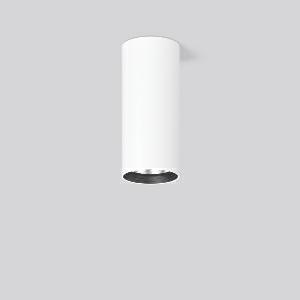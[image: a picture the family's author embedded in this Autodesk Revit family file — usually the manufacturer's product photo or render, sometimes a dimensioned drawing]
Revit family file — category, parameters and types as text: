
# Revit family: heledon_mini_a_931209_002_2_76_af3e
name_source: partatom
category: Lighting Fixtures
units: mm (PartAtom-declared; Revit-internal decimal feet)

## family parameters
Cut with Voids When Loaded = No
Host = Face
Light Source = No
Part Type = Normal
Room Calculation Point = No
Round Connector Dimension = Use Diameter
Shared = No

## types (1)
- HELEDON mini A (1 x LED Modul 927, 3300 lm, 2700)
    Apparent Load = 29 VA
    Approval mark = CE
    CIE Flux Codes = 99 100 100 100 100
    Color Rendering = 92
    Color Temperature = 2700
    Default Elevation = 1800 mm
    Description = Series: HELEDON mini
Cylindrical surface-mounted downlight. Housing: die-cast aluminium, powder-coated. Internal ceiling frame polycarbonate with bayonet mounting. Black plastic ring and recessed LED to prevent glare from the side. Optical assembly with reflector made of MIRO-Silver with 98% total light reflection for outstanding efficiency - can be changed without tools. Best colour rendering index Ra>90. Suitable for Ceiling mounting. Easy installation with a separate ceiling frame with bayonet mounting and plug connection. Driver integrated. Connected via plug-in connector. High quality converter without flickering and stroboscopic effect. The following accessories can be mounted without use of tools: interchangeable lenses, decorative glasses, honeycomb louvre, clear and frosted diffusers, white interchangeable plastic ring. 
Colour: traffic white, matt (RAL 9016)
Diameter: 87 mm
Height: 197 mm
Lamp: LED
Socket: without socket
Colour temperature: 2700K
Colour rendering index (CRI): 92
System power: 29 W
Rated luminous flux: 3300 lm
Luminous efficiency: 114 lm/W
Control gear: Converter, dimmable, DALI
Protection class: I
Type of protection: IP 20
    Height = 197 mm
    Lamp = 1 x LED Modul 927
    Lamp Light Flux = 3300 lm
    Lamp count = 1
    Length = 87 mm
    Lifetime = 50000 h
    Luminous efficacy = 114 lm/W
    Manufacturer = RZB
    ModVariant = No
    Model = 931209.002.2.76
    Mounting Place = Ceiling
    Mounting Type = Surface mounted
    Number of Poles = 1
    OnlyDefault = Yes
    Power Factor = 1
    Product Name = HELEDON mini A
    Product group = Surface mounted downlights
    ProductGroupID = 302
    Protection Class = Protection class I
    Protection Degree = IP 20
    RLX_Detail_Level = 1
    RLX_Emergency_Light_Flux = 0 lm
    RLX_Emergency_Type = 0
    RLX_Emergency_Type_DB = No
    RlxData = <blob elided: 105721 chars, md5=2c121c77>
    Socket = socket
    Standby Power = 0 W
    System Light Flux = 3300 lm
    System Power = 29 W
    Type Comments = Product without accessories
    Type Image = 931188.002.jpg
    URL = http://relux.com
    VarID = ---
    Voltage = 230 V
    Voltage Range = 220-240 V
    Weight = 0.00 kg
    Width = 0 mm  [stored 0 ft]

note: [stored X ft] marks values corroborated as IEEE doubles in the binary element streams (Revit-internal decimal feet)

## geometry (parser evidence)
native form markers: Blend x4, Sweep x10
no freeform markers — native parametric forms only
